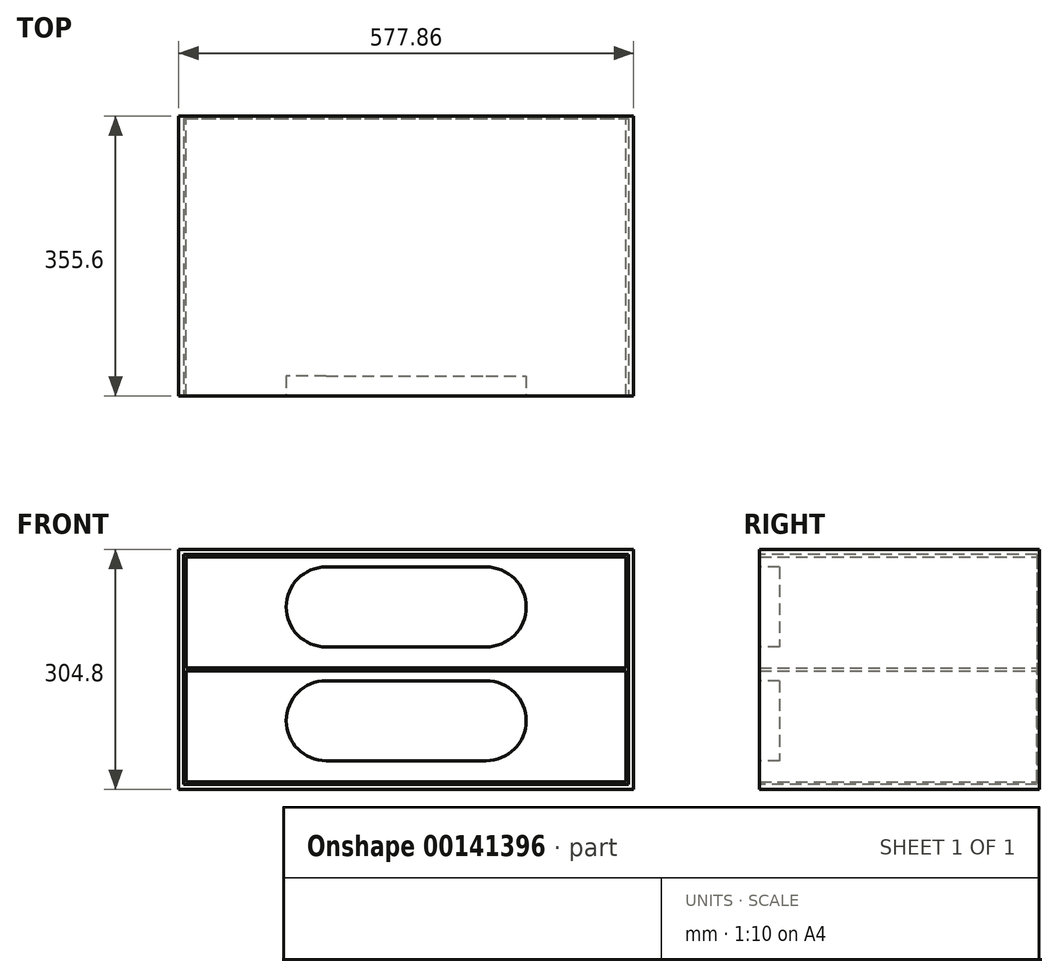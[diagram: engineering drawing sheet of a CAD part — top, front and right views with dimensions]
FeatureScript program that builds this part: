
annotation { "Feature Type Name" : "Feature", "Feature Type Description" : "" }
export const myFeature = defineFeature(function(context is Context, id is Id, definition is map)
    precondition{}
    {
        {
            var Q0;
            Q0=qCreatedBy(makeId("Top.planeOp"),FACE);
            var sketch = newSketch(context, id + "F0", { "sketchPlane" : qUnion([Q0])});
            skLineSegment(sketch, "E0.bottom", {"start": v(-288.93, 177.8) * mm, "end": v(288.93, 177.8) * mm});
            skLineSegment(sketch, "E0.top", {"start": v(-288.93, -177.8) * mm, "end": v(288.93, -177.8) * mm});
            skLineSegment(sketch, "E0.left", {"start": v(-288.93, 177.8) * mm, "end": v(-288.93, -177.8) * mm});
            skLineSegment(sketch, "E0.right", {"start": v(288.93, 177.8) * mm, "end": v(288.93, -177.8) * mm});
            skPoint(sketch, "E0.middle", {"position": v(0, 0) * mm});
            skSolve(sketch);
        }
        {
            var Q0;
            Q0 = qSketchRegion(id + "F0", true);
            extrude(context, id + "F1", {"entities" : qUnion([Q0]), "depth" : 304.8 * mm});
        }
        {
            var Q0;
            Q0=makeQuery(id+"F1.opExtrude","SWEPT_FACE",FACE,{"disambiguationData":[OSD([sQuery(id+"F0.wireOp",EDGE,"E0.top")])]});
            var sketch = newSketch(context, id + "F2", { "sketchPlane" : qUnion([Q0])});
            skLineSegment(sketch, "E1.bottom", {"start": v(-282.58, 298.45) * mm, "end": v(282.58, 298.45) * mm});
            skLineSegment(sketch, "E1.top", {"start": v(-282.58, 6.35) * mm, "end": v(282.58, 6.35) * mm});
            skLineSegment(sketch, "E1.left", {"start": v(-282.58, 298.45) * mm, "end": v(-282.58, 6.35) * mm});
            skLineSegment(sketch, "E1.right", {"start": v(282.58, 298.45) * mm, "end": v(282.58, 6.35) * mm});
            skPoint(sketch, "E1.middle", {"position": v(0, 152.4) * mm});
            skPoint(sketch, "E1.middle.positionSnap0", {"position": v(-288.93, 152.4) * mm});
            skPoint(sketch, "E1.centerSnap0", {"position": v(-288.93, 152.4) * mm});
            skSolve(sketch);
        }
        {
            var Q0;
            Q0 = qSketchRegion(id + "F2", true);
            extrude(context, id + "F3", {"entities" : qUnion([Q0]), "operationType" : NewBodyOperationType.REMOVE, "oppositeDirection" : true, "depth" : 352.42 * mm});
        }
        {
            var Q0;
            Q0=makeQuery(id+"F3.boolean.opBoolean","COPY",FACE,{"derivedFrom":makeQuery(id+"F3.opExtrude","CAP_FACE",FACE,{"disambiguationData":[OSD([sQuery(id+"F2.wireOp",EDGE,"E1.bottom"),sQuery(id+"F2.wireOp",EDGE,"E1.top"),sQuery(id+"F2.wireOp",EDGE,"E1.left"),sQuery(id+"F2.wireOp",EDGE,"E1.right")])],"isStart":false})});
            var sketch = newSketch(context, id + "F4", { "sketchPlane" : qUnion([Q0])});
            skLineSegment(sketch, "E2.bottom", {"start": v(-279.4, 295.28) * mm, "end": v(279.4, 295.28) * mm});
            skLineSegment(sketch, "E2.top", {"start": v(-279.4, 154.05) * mm, "end": v(279.4, 154.05) * mm});
            skLineSegment(sketch, "E2.left", {"start": v(-279.4, 295.28) * mm, "end": v(-279.4, 154.05) * mm});
            skLineSegment(sketch, "E2.right", {"start": v(279.4, 295.28) * mm, "end": v(279.4, 154.05) * mm});
            skLineSegment(sketch, "E3.bottom", {"start": v(-279.4, 9.53) * mm, "end": v(279.4, 9.53) * mm});
            skLineSegment(sketch, "E3.top", {"start": v(-279.4, 150.75) * mm, "end": v(279.4, 150.75) * mm});
            skLineSegment(sketch, "E3.left", {"start": v(-279.4, 9.53) * mm, "end": v(-279.4, 150.75) * mm});
            skLineSegment(sketch, "E3.right", {"start": v(279.4, 9.53) * mm, "end": v(279.4, 150.75) * mm});
            skSolve(sketch);
        }
        {
            var Q0;
            Q0 = qSketchRegion(id + "F4", true);
            extrude(context, id + "F5", {"entities" : qUnion([Q0]), "operationType" : NewBodyOperationType.ADD, "depth" : 352.42 * mm});
        }
        {
            var Q0;
            Q0=makeQuery(id+"F5.opExtrude","CAP_FACE",FACE,{"disambiguationData":[OSD([sQuery(id+"F4.wireOp",EDGE,"E2.bottom"),sQuery(id+"F4.wireOp",EDGE,"E2.top"),sQuery(id+"F4.wireOp",EDGE,"E2.left"),sQuery(id+"F4.wireOp",EDGE,"E2.right")])],"isStart":false});
            var sketch = newSketch(context, id + "F6", { "sketchPlane" : qUnion([Q0])});
            skLineSegment(sketch, "E4.bottom", {"start": v(-101.6, 282.58) * mm, "end": v(101.6, 282.58) * mm});
            skLineSegment(sketch, "E4.top", {"start": v(-101.6, 180.97) * mm, "end": v(101.6, 180.97) * mm});
            skLineSegment(sketch, "E5", {"start": v(0, 0) * mm, "end": v(0, 295.28) * mm});
            skArc(sketch, "E6", {"start": v(-101.6, 282.58) * mm, "mid": v(-152.4, 231.77) * mm, "end": v(-101.6, 180.97) * mm});
            skArc(sketch, "E7", {"start": v(101.6, 180.97) * mm, "mid": v(152.4, 231.78) * mm, "end": v(101.6, 282.58) * mm});
            skLineSegment(sketch, "E8.bottom", {"start": v(-101.6, 138.05) * mm, "end": v(101.6, 138.05) * mm});
            skLineSegment(sketch, "E8.top", {"start": v(-101.6, 36.45) * mm, "end": v(101.6, 36.45) * mm});
            skArc(sketch, "E9", {"start": v(-101.6, 138.05) * mm, "mid": v(-152.4, 87.25) * mm, "end": v(-101.6, 36.45) * mm});
            skArc(sketch, "E10", {"start": v(101.6, 36.45) * mm, "mid": v(152.4, 87.25) * mm, "end": v(101.6, 138.05) * mm});
            skSolve(sketch);
        }
        {
            var Q0;
            Q0 = qSketchRegion(id + "F6", true);
            extrude(context, id + "F7", {"entities" : qUnion([Q0]), "operationType" : NewBodyOperationType.REMOVE, "oppositeDirection" : true, "depth" : 25.4 * mm});
        }
    });
